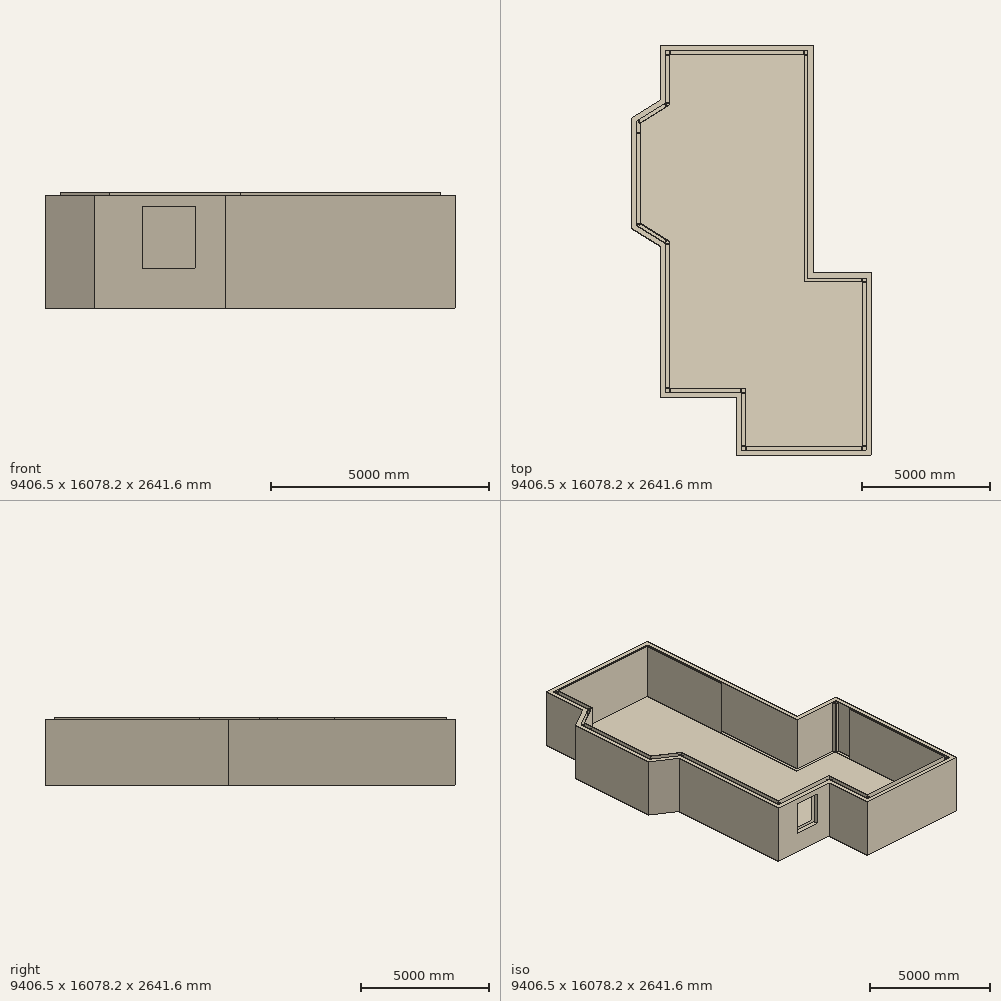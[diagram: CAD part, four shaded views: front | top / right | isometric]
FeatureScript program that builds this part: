
annotation { "Feature Type Name" : "Feature", "Feature Type Description" : "" }
export const myFeature = defineFeature(function(context is Context, id is Id, definition is map)
    precondition{}
    {
        {
            var Q0;
            Q0=qCreatedBy(makeId("Top.planeOp"),FACE);
            var sketch = newSketch(context, id + "F0", { "sketchPlane" : qUnion([Q0])});
            skLineSegment(sketch, "E0", {"start": v(-8280.4, 16078.2) * mm, "end": v(-2286, 16078.2) * mm});
            skLineSegment(sketch, "E1", {"start": v(-2286, 16078.2) * mm, "end": v(-2286, 7162.8) * mm});
            skLineSegment(sketch, "E2", {"start": v(-2286, 7162.8) * mm, "end": v(0, 7162.8) * mm});
            skLineSegment(sketch, "E3", {"start": v(0, 7162.8) * mm, "end": v(0, 0) * mm});
            skLineSegment(sketch, "E4", {"start": v(0, 0) * mm, "end": v(-5283.2, 0) * mm});
            skLineSegment(sketch, "E5", {"start": v(-5283.2, 0) * mm, "end": v(-5283.2, 2286) * mm});
            skLineSegment(sketch, "E6", {"start": v(-5283.2, 2286) * mm, "end": v(-8280.4, 2286) * mm});
            skLineSegment(sketch, "E7", {"start": v(-8280.4, 2286) * mm, "end": v(-8280.4, 8201.03) * mm});
            skLineSegment(sketch, "E8", {"start": v(-8280.4, 8201.03) * mm, "end": v(-9406.5, 8900.32) * mm});
            skLineSegment(sketch, "E9", {"start": v(-9406.5, 8900.32) * mm, "end": v(-9406.5, 13223.08) * mm});
            skLineSegment(sketch, "E10", {"start": v(-9406.5, 13223.08) * mm, "end": v(-8280.4, 13922.38) * mm});
            skLineSegment(sketch, "E11", {"start": v(-8280.4, 13922.38) * mm, "end": v(-8280.4, 16078.2) * mm});
            skSolve(sketch);
        }
        {
            var Q0;
            Q0=qSketchRegion(id+"F0",true);
            extrude(context, id + "F1", {"entities" : qUnion([Q0]), "depth" : 2578.1 * mm});
        }
        {
            var Q0;
            Q0=makeQuery(id+"F1.opExtrude","CAP_FACE",FACE,{"disambiguationData":[OSD([sQuery(id+"F0.wireOp",EDGE,"E0"),sQuery(id+"F0.wireOp",EDGE,"E1"),sQuery(id+"F0.wireOp",EDGE,"E2"),sQuery(id+"F0.wireOp",EDGE,"E3"),sQuery(id+"F0.wireOp",EDGE,"E4"),sQuery(id+"F0.wireOp",EDGE,"E5"),sQuery(id+"F0.wireOp",EDGE,"E6"),sQuery(id+"F0.wireOp",EDGE,"E7"),sQuery(id+"F0.wireOp",EDGE,"E8"),sQuery(id+"F0.wireOp",EDGE,"E9"),sQuery(id+"F0.wireOp",EDGE,"E10"),sQuery(id+"F0.wireOp",EDGE,"E11")])],"isStart":false});
            shell(context, id + "F2", {"entities" : qUnion([Q0]), "thickness" : 203.2 * mm});
        }
        {
            var Q0;
            Q0=makeQuery(id+"F2.opShell","OFFSET_FACE",FACE,{"disambiguationData":[OSD([sQuery(id+"F0.wireOp",EDGE,"E6")])]});
            var sketch = newSketch(context, id + "F3", { "sketchPlane" : qUnion([Q0])});
            skLineSegment(sketch, "E12.bottom", {"start": v(5969, 2324.1) * mm, "end": v(7188.2, 2324.1) * mm});
            skLineSegment(sketch, "E12.top", {"start": v(5969, 901.7) * mm, "end": v(7188.2, 901.7) * mm});
            skLineSegment(sketch, "E12.left", {"start": v(5969, 2324.1) * mm, "end": v(5969, 901.7) * mm});
            skLineSegment(sketch, "E12.right", {"start": v(7188.2, 2324.1) * mm, "end": v(7188.2, 901.7) * mm});
            skPoint(sketch, "E13", {"position": v(6578.6, 2324.1) * mm});
            skSolve(sketch);
        }
        {
            var Q0;
            Q0=makeQuery(id+"F2.opShell","OFFSET_FACE",FACE,{"disambiguationData":[OSD([sQuery(id+"F0.wireOp",EDGE,"E0"),sQuery(id+"F0.wireOp",EDGE,"E1"),sQuery(id+"F0.wireOp",EDGE,"E2"),sQuery(id+"F0.wireOp",EDGE,"E3"),sQuery(id+"F0.wireOp",EDGE,"E4"),sQuery(id+"F0.wireOp",EDGE,"E5"),sQuery(id+"F0.wireOp",EDGE,"E6"),sQuery(id+"F0.wireOp",EDGE,"E7"),sQuery(id+"F0.wireOp",EDGE,"E8"),sQuery(id+"F0.wireOp",EDGE,"E9"),sQuery(id+"F0.wireOp",EDGE,"E10"),sQuery(id+"F0.wireOp",EDGE,"E11")])]});
            var sketch = newSketch(context, id + "F4", { "sketchPlane" : qUnion([Q0])});
            skLineSegment(sketch, "E14.bottom", {"start": v(-8077.2, 13811.9) * mm, "end": v(-7937.5, 13811.9) * mm});
            skLineSegment(sketch, "E14.top", {"start": v(-8077.2, 13850) * mm, "end": v(-7937.5, 13850) * mm});
            skLineSegment(sketch, "E14.left", {"start": v(-8077.2, 13811.9) * mm, "end": v(-8077.2, 13850) * mm});
            skLineSegment(sketch, "E14.right", {"start": v(-7937.5, 13811.9) * mm, "end": v(-7937.5, 13850) * mm});
            skLineSegment(sketch, "E15.bottom", {"start": v(-7934.96, 15875) * mm, "end": v(-7896.86, 15875) * mm});
            skLineSegment(sketch, "E15.top", {"start": v(-7934.96, 15735.3) * mm, "end": v(-7896.86, 15735.3) * mm});
            skLineSegment(sketch, "E15.left", {"start": v(-7934.96, 15875) * mm, "end": v(-7934.96, 15735.3) * mm});
            skLineSegment(sketch, "E15.right", {"start": v(-7896.86, 15875) * mm, "end": v(-7896.86, 15735.3) * mm});
            skLineSegment(sketch, "E16.bottom", {"start": v(-8077.2, 15694.66) * mm, "end": v(-7937.5, 15694.66) * mm});
            skLineSegment(sketch, "E16.top", {"start": v(-8077.2, 15732.76) * mm, "end": v(-7937.5, 15732.76) * mm});
            skLineSegment(sketch, "E16.left", {"start": v(-8077.2, 15694.66) * mm, "end": v(-8077.2, 15732.76) * mm});
            skLineSegment(sketch, "E16.right", {"start": v(-7937.5, 15694.66) * mm, "end": v(-7937.5, 15732.76) * mm});
            skLineSegment(sketch, "E17.bottom", {"start": v(-2631.44, 15875) * mm, "end": v(-2669.54, 15875) * mm});
            skLineSegment(sketch, "E17.top", {"start": v(-2631.44, 15735.3) * mm, "end": v(-2669.54, 15735.3) * mm});
            skLineSegment(sketch, "E17.left", {"start": v(-2631.44, 15875) * mm, "end": v(-2631.44, 15735.3) * mm});
            skLineSegment(sketch, "E17.right", {"start": v(-2669.54, 15875) * mm, "end": v(-2669.54, 15735.3) * mm});
            skLineSegment(sketch, "E18.bottom", {"start": v(-2489.2, 15694.66) * mm, "end": v(-2628.9, 15694.66) * mm});
            skLineSegment(sketch, "E18.top", {"start": v(-2489.2, 15732.76) * mm, "end": v(-2628.9, 15732.76) * mm});
            skLineSegment(sketch, "E18.left", {"start": v(-2489.2, 15694.66) * mm, "end": v(-2489.2, 15732.76) * mm});
            skLineSegment(sketch, "E18.right", {"start": v(-2628.9, 15694.66) * mm, "end": v(-2628.9, 15732.76) * mm});
            skLineSegment(sketch, "E19", {"start": v(-8078.22, 13808.73) * mm, "end": v(-8110.59, 13788.64) * mm});
            skLineSegment(sketch, "E20", {"start": v(-8110.59, 13788.64) * mm, "end": v(-8036.89, 13669.96) * mm});
            skLineSegment(sketch, "E21", {"start": v(-8036.89, 13669.96) * mm, "end": v(-8004.52, 13690.06) * mm});
            skLineSegment(sketch, "E22", {"start": v(-8004.52, 13690.06) * mm, "end": v(-8078.22, 13808.73) * mm});
            skLineSegment(sketch, "E23.bottom", {"start": v(-9203.3, 12669.47) * mm, "end": v(-9063.6, 12669.47) * mm});
            skLineSegment(sketch, "E23.top", {"start": v(-9203.3, 12631.37) * mm, "end": v(-9063.6, 12631.37) * mm});
            skLineSegment(sketch, "E23.left", {"start": v(-9203.3, 12669.47) * mm, "end": v(-9203.3, 12631.37) * mm});
            skLineSegment(sketch, "E23.right", {"start": v(-9063.6, 12669.47) * mm, "end": v(-9063.6, 12631.37) * mm});
            skLineSegment(sketch, "E24", {"start": v(-9162.3, 13135.53) * mm, "end": v(-9129.94, 13155.63) * mm});
            skLineSegment(sketch, "E25", {"start": v(-9129.94, 13155.63) * mm, "end": v(-9056.24, 13036.95) * mm});
            skLineSegment(sketch, "E26", {"start": v(-9056.24, 13036.95) * mm, "end": v(-9088.6, 13016.85) * mm});
            skLineSegment(sketch, "E27", {"start": v(-9088.6, 13016.85) * mm, "end": v(-9162.3, 13135.53) * mm});
            skLineSegment(sketch, "E28", {"start": v(-9162.3, 8987.87) * mm, "end": v(-9088.6, 9106.55) * mm});
            skLineSegment(sketch, "E29", {"start": v(-9088.6, 9106.55) * mm, "end": v(-9056.24, 9086.45) * mm});
            skLineSegment(sketch, "E30", {"start": v(-9056.24, 9086.45) * mm, "end": v(-9129.94, 8967.77) * mm});
            skLineSegment(sketch, "E31", {"start": v(-9129.94, 8967.77) * mm, "end": v(-9162.3, 8987.87) * mm});
            skLineSegment(sketch, "E32", {"start": v(-8109.57, 8334.13) * mm, "end": v(-8077.2, 8314.03) * mm});
            skLineSegment(sketch, "E33", {"start": v(-8077.2, 8314.03) * mm, "end": v(-8003.5, 8432.71) * mm});
            skLineSegment(sketch, "E34", {"start": v(-8003.5, 8432.71) * mm, "end": v(-8035.87, 8452.81) * mm});
            skLineSegment(sketch, "E35", {"start": v(-8035.87, 8452.81) * mm, "end": v(-8109.57, 8334.13) * mm});
            skLineSegment(sketch, "E36.bottom", {"start": v(-9203.3, 9061.59) * mm, "end": v(-9063.6, 9061.59) * mm});
            skLineSegment(sketch, "E36.top", {"start": v(-9203.3, 9099.69) * mm, "end": v(-9063.6, 9099.69) * mm});
            skLineSegment(sketch, "E36.left", {"start": v(-9203.3, 9061.59) * mm, "end": v(-9203.3, 9099.69) * mm});
            skLineSegment(sketch, "E36.right", {"start": v(-9063.6, 9061.59) * mm, "end": v(-9063.6, 9099.69) * mm});
            skLineSegment(sketch, "E37.bottom", {"start": v(-8077.2, 8311.5) * mm, "end": v(-7937.5, 8311.5) * mm});
            skLineSegment(sketch, "E37.top", {"start": v(-8077.2, 8273.4) * mm, "end": v(-7937.5, 8273.4) * mm});
            skLineSegment(sketch, "E37.left", {"start": v(-8077.2, 8311.5) * mm, "end": v(-8077.2, 8273.4) * mm});
            skLineSegment(sketch, "E37.right", {"start": v(-7937.5, 8311.5) * mm, "end": v(-7937.5, 8273.4) * mm});
            skLineSegment(sketch, "E38.bottom", {"start": v(-8077.2, 2631.44) * mm, "end": v(-7937.5, 2631.44) * mm});
            skLineSegment(sketch, "E38.top", {"start": v(-8077.2, 2669.54) * mm, "end": v(-7937.5, 2669.54) * mm});
            skLineSegment(sketch, "E38.left", {"start": v(-8077.2, 2631.44) * mm, "end": v(-8077.2, 2669.54) * mm});
            skLineSegment(sketch, "E38.right", {"start": v(-7937.5, 2631.44) * mm, "end": v(-7937.5, 2669.54) * mm});
            skLineSegment(sketch, "E39.bottom", {"start": v(-7896.86, 2489.2) * mm, "end": v(-7934.96, 2489.2) * mm});
            skLineSegment(sketch, "E39.top", {"start": v(-7896.86, 2628.9) * mm, "end": v(-7934.96, 2628.9) * mm});
            skLineSegment(sketch, "E39.left", {"start": v(-7896.86, 2489.2) * mm, "end": v(-7896.86, 2628.9) * mm});
            skLineSegment(sketch, "E39.right", {"start": v(-7934.96, 2489.2) * mm, "end": v(-7934.96, 2628.9) * mm});
            skLineSegment(sketch, "E40.bottom", {"start": v(-5082.54, 2489.2) * mm, "end": v(-5120.64, 2489.2) * mm});
            skLineSegment(sketch, "E40.top", {"start": v(-5082.54, 2628.9) * mm, "end": v(-5120.64, 2628.9) * mm});
            skLineSegment(sketch, "E40.left", {"start": v(-5082.54, 2489.2) * mm, "end": v(-5082.54, 2628.9) * mm});
            skLineSegment(sketch, "E40.right", {"start": v(-5120.64, 2489.2) * mm, "end": v(-5120.64, 2628.9) * mm});
            skLineSegment(sketch, "E41.top", {"start": v(-5080, 2448.56) * mm, "end": v(-4940.3, 2448.56) * mm});
            skLineSegment(sketch, "E41.right", {"start": v(-4940.3, 2486.66) * mm, "end": v(-4940.3, 2448.56) * mm});
            skLineSegment(sketch, "E42.bottom", {"start": v(-5080, 345.44) * mm, "end": v(-4940.3, 345.44) * mm});
            skLineSegment(sketch, "E42.top", {"start": v(-5080, 383.54) * mm, "end": v(-4940.3, 383.54) * mm});
            skLineSegment(sketch, "E42.left", {"start": v(-5080, 345.44) * mm, "end": v(-5080, 383.54) * mm});
            skLineSegment(sketch, "E42.right", {"start": v(-4940.3, 345.44) * mm, "end": v(-4940.3, 383.54) * mm});
            skLineSegment(sketch, "E43.bottom", {"start": v(-4937.76, 203.2) * mm, "end": v(-4899.66, 203.2) * mm});
            skLineSegment(sketch, "E43.top", {"start": v(-4937.76, 342.9) * mm, "end": v(-4899.66, 342.9) * mm});
            skLineSegment(sketch, "E43.left", {"start": v(-4937.76, 203.2) * mm, "end": v(-4937.76, 342.9) * mm});
            skLineSegment(sketch, "E43.right", {"start": v(-4899.66, 203.2) * mm, "end": v(-4899.66, 342.9) * mm});
            skLineSegment(sketch, "E44.bottom", {"start": v(-383.54, 203.2) * mm, "end": v(-345.44, 203.2) * mm});
            skLineSegment(sketch, "E44.top", {"start": v(-383.54, 342.9) * mm, "end": v(-345.44, 342.9) * mm});
            skLineSegment(sketch, "E44.left", {"start": v(-383.54, 203.2) * mm, "end": v(-383.54, 342.9) * mm});
            skLineSegment(sketch, "E44.right", {"start": v(-345.44, 203.2) * mm, "end": v(-345.44, 342.9) * mm});
            skLineSegment(sketch, "E45.bottom", {"start": v(-203.2, 345.44) * mm, "end": v(-342.9, 345.44) * mm});
            skLineSegment(sketch, "E45.top", {"start": v(-203.2, 383.54) * mm, "end": v(-342.9, 383.54) * mm});
            skLineSegment(sketch, "E45.left", {"start": v(-203.2, 345.44) * mm, "end": v(-203.2, 383.54) * mm});
            skLineSegment(sketch, "E45.right", {"start": v(-342.9, 345.44) * mm, "end": v(-342.9, 383.54) * mm});
            skLineSegment(sketch, "E46.bottom", {"start": v(-203.2, 6779.26) * mm, "end": v(-342.9, 6779.26) * mm});
            skLineSegment(sketch, "E46.top", {"start": v(-203.2, 6817.36) * mm, "end": v(-342.9, 6817.36) * mm});
            skLineSegment(sketch, "E46.left", {"start": v(-203.2, 6779.26) * mm, "end": v(-203.2, 6817.36) * mm});
            skLineSegment(sketch, "E46.right", {"start": v(-342.9, 6779.26) * mm, "end": v(-342.9, 6817.36) * mm});
            skLineSegment(sketch, "E47.bottom", {"start": v(-345.44, 6959.6) * mm, "end": v(-383.54, 6959.6) * mm});
            skLineSegment(sketch, "E47.top", {"start": v(-345.44, 6819.9) * mm, "end": v(-383.54, 6819.9) * mm});
            skLineSegment(sketch, "E47.left", {"start": v(-345.44, 6959.6) * mm, "end": v(-345.44, 6819.9) * mm});
            skLineSegment(sketch, "E47.right", {"start": v(-383.54, 6959.6) * mm, "end": v(-383.54, 6819.9) * mm});
            skLineSegment(sketch, "E48", {"start": v(-4940.3, 2486.66) * mm, "end": v(-5080, 2486.66) * mm});
            skLineSegment(sketch, "E49", {"start": v(-5080, 2486.66) * mm, "end": v(-5080, 2448.56) * mm});
            skLineSegment(sketch, "E50", {"start": v(-9203.3, 13110.07) * mm, "end": v(-9045.7, 12987.43) * mm, "construction": true});
            skLineSegment(sketch, "E51", {"start": v(-9045.7, 12987.43) * mm, "end": v(-9104.83, 13171.22) * mm, "construction": true});
            skLineSegment(sketch, "E52", {"start": v(-9104.83, 13171.22) * mm, "end": v(-9203.3, 12968.55) * mm, "construction": true});
            skLineSegment(sketch, "E53", {"start": v(-9203.3, 12968.55) * mm, "end": v(-9045.7, 12987.43) * mm, "construction": true});
            skSolve(sketch);
        }
        {
            var Q0;
            Q0=qSketchRegion(id+"F3",true);
            var Q1;
            Q1=makeQuery(id+"FwcOo8eikqoZCvb_1.opExtrude","SWEPT_FACE",FACE,{"disambiguationData":[OSD([sQuery(id+"F7.wireOp",EDGE,"E55.top"),sQuery(id+"F7.wireOp",EDGE,"E63")])]});
            extrude(context, id + "F5", {"entities" : qUnion([Q0]), "operationType" : NewBodyOperationType.REMOVE, "endBound" : BoundingType.UP_TO_NEXT, "oppositeDirection" : true, "depth" : 25.4 * mm});
        }
        {
            var Q0;
            Q0=qSketchRegion(id+"F4",true);
            extrude(context, id + "F6", {"entities" : qUnion([Q0]), "operationType" : NewBodyOperationType.ADD, "depth" : 2349.5 * mm});
        }
        {
            var Q0;
            Q0=makeQuery(id+"F2.opShell","OFFSET_FACE",FACE,{"disambiguationData":[OSD([sQuery(id+"F0.wireOp",EDGE,"E0"),sQuery(id+"F0.wireOp",EDGE,"E1"),sQuery(id+"F0.wireOp",EDGE,"E2"),sQuery(id+"F0.wireOp",EDGE,"E3"),sQuery(id+"F0.wireOp",EDGE,"E4"),sQuery(id+"F0.wireOp",EDGE,"E5"),sQuery(id+"F0.wireOp",EDGE,"E6"),sQuery(id+"F0.wireOp",EDGE,"E7"),sQuery(id+"F0.wireOp",EDGE,"E8"),sQuery(id+"F0.wireOp",EDGE,"E9"),sQuery(id+"F0.wireOp",EDGE,"E10"),sQuery(id+"F0.wireOp",EDGE,"E11")])]});
            var sketch = newSketch(context, id + "F7", { "sketchPlane" : qUnion([Q0])});
            skLineSegment(sketch, "E54.bottom", {"start": v(-7937.5, 8391.73) * mm, "end": v(-7924.8, 8391.73) * mm, "construction": true});
            skLineSegment(sketch, "E54.top", {"start": v(-7937.5, 2641.6) * mm, "end": v(-7924.8, 2641.6) * mm, "construction": true});
            skLineSegment(sketch, "E54.left", {"start": v(-7937.5, 8391.73) * mm, "end": v(-7937.5, 2641.6) * mm});
            skLineSegment(sketch, "E54.right", {"start": v(-7924.8, 8391.73) * mm, "end": v(-7924.8, 2641.6) * mm});
            skLineSegment(sketch, "E55.bottom", {"start": v(-7924.8, 2628.9) * mm, "end": v(-4940.3, 2628.9) * mm});
            skLineSegment(sketch, "E55.top", {"start": v(-7924.8, 2641.6) * mm, "end": v(-4940.3, 2641.6) * mm});
            skLineSegment(sketch, "E55.left", {"start": v(-7924.8, 2628.9) * mm, "end": v(-7924.8, 2641.6) * mm, "construction": true});
            skLineSegment(sketch, "E55.right", {"start": v(-4940.3, 2628.9) * mm, "end": v(-4940.3, 2641.6) * mm, "construction": true});
            skLineSegment(sketch, "E56", {"start": v(-7924.8, 2628.9) * mm, "end": v(-7937.5, 2628.9) * mm});
            skLineSegment(sketch, "E57", {"start": v(-7937.5, 2628.9) * mm, "end": v(-7937.5, 2641.6) * mm});
            skLineSegment(sketch, "E58.bottom", {"start": v(-4940.3, 2628.9) * mm, "end": v(-4927.6, 2628.9) * mm, "construction": true});
            skLineSegment(sketch, "E58.top", {"start": v(-4940.3, 355.6) * mm, "end": v(-4927.6, 355.6) * mm, "construction": true});
            skLineSegment(sketch, "E58.left", {"start": v(-4940.3, 2628.9) * mm, "end": v(-4940.3, 355.6) * mm});
            skLineSegment(sketch, "E58.right", {"start": v(-4927.6, 2628.9) * mm, "end": v(-4927.6, 355.6) * mm});
            skLineSegment(sketch, "E59.bottom", {"start": v(-4927.6, 342.9) * mm, "end": v(-355.6, 342.9) * mm});
            skLineSegment(sketch, "E59.top", {"start": v(-4927.6, 355.6) * mm, "end": v(-355.6, 355.6) * mm});
            skLineSegment(sketch, "E59.left", {"start": v(-4927.6, 342.9) * mm, "end": v(-4927.6, 355.6) * mm, "construction": true});
            skLineSegment(sketch, "E59.right", {"start": v(-355.6, 342.9) * mm, "end": v(-355.6, 355.6) * mm, "construction": true});
            skLineSegment(sketch, "E60", {"start": v(-4940.3, 355.6) * mm, "end": v(-4940.3, 342.9) * mm});
            skLineSegment(sketch, "E61", {"start": v(-4940.3, 342.9) * mm, "end": v(-4927.6, 342.9) * mm});
            skLineSegment(sketch, "E62", {"start": v(-4927.6, 2628.9) * mm, "end": v(-4927.6, 2641.6) * mm});
            skLineSegment(sketch, "E63", {"start": v(-4940.3, 2641.6) * mm, "end": v(-4927.6, 2641.6) * mm});
            skLineSegment(sketch, "E64.bottom", {"start": v(-355.6, 355.6) * mm, "end": v(-342.9, 355.6) * mm, "construction": true});
            skLineSegment(sketch, "E64.top", {"start": v(-355.6, 6019.58) * mm, "end": v(-342.9, 6019.58) * mm});
            skLineSegment(sketch, "E64.left", {"start": v(-355.6, 355.6) * mm, "end": v(-355.6, 6019.58) * mm});
            skLineSegment(sketch, "E64.right", {"start": v(-342.9, 355.6) * mm, "end": v(-342.9, 6019.58) * mm});
            skLineSegment(sketch, "E65", {"start": v(-355.6, 342.9) * mm, "end": v(-342.9, 342.9) * mm});
            skLineSegment(sketch, "E66", {"start": v(-342.9, 342.9) * mm, "end": v(-342.9, 355.6) * mm});
            skLineSegment(sketch, "E67", {"start": v(-7937.5, 8391.73) * mm, "end": v(-9063.6, 9091.02) * mm});
            skLineSegment(sketch, "E68", {"start": v(-9063.6, 9091.02) * mm, "end": v(-9063.6, 13032.38) * mm});
            skLineSegment(sketch, "E69", {"start": v(-9063.6, 13032.38) * mm, "end": v(-7937.5, 13731.67) * mm});
            skLineSegment(sketch, "E70", {"start": v(-7937.5, 13731.67) * mm, "end": v(-7937.5, 15735.3) * mm});
            skLineSegment(sketch, "E71", {"start": v(-7937.5, 15735.3) * mm, "end": v(-2628.9, 15735.3) * mm});
            skLineSegment(sketch, "E72", {"start": v(-2628.9, 15735.3) * mm, "end": v(-2628.9, 11339.58) * mm});
            skLineSegment(sketch, "E73", {"start": v(-2628.9, 11339.58) * mm, "end": v(-2641.6, 11339.58) * mm});
            skLineSegment(sketch, "E74", {"start": v(-2641.6, 11339.58) * mm, "end": v(-2641.6, 15722.6) * mm});
            skLineSegment(sketch, "E75", {"start": v(-2641.6, 15722.6) * mm, "end": v(-7924.8, 15722.6) * mm});
            skLineSegment(sketch, "E76", {"start": v(-7924.8, 15722.6) * mm, "end": v(-7924.8, 13724.61) * mm});
            skLineSegment(sketch, "E77", {"start": v(-7924.8, 13724.61) * mm, "end": v(-9050.9, 13025.32) * mm});
            skLineSegment(sketch, "E78", {"start": v(-9050.9, 13025.32) * mm, "end": v(-9050.9, 9098.08) * mm});
            skLineSegment(sketch, "E79", {"start": v(-9050.9, 9098.08) * mm, "end": v(-7924.8, 8398.79) * mm});
            skLineSegment(sketch, "E80", {"start": v(-8493.85, 8752.16) * mm, "end": v(-8500.55, 8741.37) * mm, "construction": true});
            skLineSegment(sketch, "E81", {"start": v(-9063.6, 11061.7) * mm, "end": v(-9050.9, 11061.7) * mm, "construction": true});
            skLineSegment(sketch, "E82", {"start": v(-8487.85, 13374.97) * mm, "end": v(-8494.55, 13385.75) * mm, "construction": true});
            skLineSegment(sketch, "E83", {"start": v(-7924.8, 15722.6) * mm, "end": v(-7937.5, 15722.6) * mm, "construction": true});
            skLineSegment(sketch, "E84", {"start": v(-2641.6, 15735.3) * mm, "end": v(-2641.6, 15722.6) * mm, "construction": true});
            skLineSegment(sketch, "E85", {"start": v(-7924.8, 8391.73) * mm, "end": v(-7924.8, 8398.79) * mm});
            skSolve(sketch);
        }
        {
            var Q0;
            Q0=qSketchRegion(id+"F7",true);
            extrude(context, id + "F8", {"entities" : qUnion([Q0]), "depth" : 12 * 203.2 * mm});
        }
        {
            var Q0;
            Q0=qSketchRegion(id+"F3",true);
            var Q1;
            Q1=makeQuery(id+"F8.opExtrude","SWEPT_FACE",FACE,{"disambiguationData":[OSD([sQuery(id+"F7.wireOp",EDGE,"E55.top"),sQuery(id+"F7.wireOp",EDGE,"E63")])]});
            extrude(context, id + "F9", {"entities" : qUnion([Q0]), "operationType" : NewBodyOperationType.REMOVE, "endBound" : BoundingType.UP_TO_SURFACE, "endBoundEntityFace" : qUnion([Q1]), "depth" : 25.4 * mm});
        }
        {
            var Q0;
            Q0=qCreatedBy(makeId("Top.planeOp"),FACE);
            var sketch = newSketch(context, id + "F10", { "sketchPlane" : qUnion([Q0])});
            skLineSegment(sketch, "E86", {"start": v(-8077.2, 2489.2) * mm, "end": v(-8077.2, 8314.03) * mm});
            skLineSegment(sketch, "E87", {"start": v(-8077.2, 8314.03) * mm, "end": v(-9203.3, 9013.33) * mm});
            skLineSegment(sketch, "E88", {"start": v(-9203.3, 9013.33) * mm, "end": v(-9203.3, 13110.07) * mm});
            skLineSegment(sketch, "E89", {"start": v(-9203.3, 13110.07) * mm, "end": v(-8077.2, 13809.37) * mm});
            skLineSegment(sketch, "E90", {"start": v(-8077.2, 13809.37) * mm, "end": v(-8077.2, 15875) * mm});
            skLineSegment(sketch, "E91", {"start": v(-8077.2, 15875) * mm, "end": v(-2489.2, 15875) * mm});
            skLineSegment(sketch, "E92", {"start": v(-2489.2, 15875) * mm, "end": v(-2489.2, 11339.58) * mm});
            skLineSegment(sketch, "E93", {"start": v(-2489.2, 11339.58) * mm, "end": v(-2628.9, 11339.58) * mm});
            skLineSegment(sketch, "E94", {"start": v(-2628.9, 11339.58) * mm, "end": v(-2628.9, 15735.3) * mm});
            skLineSegment(sketch, "E95", {"start": v(-7937.5, 15735.3) * mm, "end": v(-7937.5, 13731.67) * mm});
            skLineSegment(sketch, "E96", {"start": v(-7937.5, 13731.67) * mm, "end": v(-9063.6, 13032.38) * mm});
            skLineSegment(sketch, "E97", {"start": v(-9063.6, 13032.38) * mm, "end": v(-9063.6, 9091.02) * mm});
            skLineSegment(sketch, "E98", {"start": v(-9063.6, 9091.02) * mm, "end": v(-7937.5, 8391.73) * mm});
            skLineSegment(sketch, "E99", {"start": v(-7937.5, 8391.73) * mm, "end": v(-7937.5, 2628.9) * mm});
            skLineSegment(sketch, "E100", {"start": v(-7937.5, 2628.9) * mm, "end": v(-4940.3, 2628.9) * mm});
            skLineSegment(sketch, "E101", {"start": v(-4940.3, 2628.9) * mm, "end": v(-4940.3, 342.9) * mm});
            skLineSegment(sketch, "E102", {"start": v(-4940.3, 342.9) * mm, "end": v(-342.9, 342.9) * mm});
            skLineSegment(sketch, "E103", {"start": v(-342.9, 342.9) * mm, "end": v(-342.9, 5526.42) * mm});
            skLineSegment(sketch, "E104", {"start": v(-342.9, 5526.42) * mm, "end": v(-203.2, 5526.42) * mm});
            skLineSegment(sketch, "E105", {"start": v(-203.2, 5526.42) * mm, "end": v(-203.2, 203.2) * mm});
            skLineSegment(sketch, "E106", {"start": v(-203.2, 203.2) * mm, "end": v(-5080, 203.2) * mm});
            skLineSegment(sketch, "E107", {"start": v(-5080, 203.2) * mm, "end": v(-5080, 2489.2) * mm});
            skLineSegment(sketch, "E108", {"start": v(-5080, 2489.2) * mm, "end": v(-8077.2, 2489.2) * mm});
            skLineSegment(sketch, "E109", {"start": v(-9203.3, 11061.7) * mm, "end": v(-9063.6, 11061.7) * mm, "construction": true});
            skLineSegment(sketch, "E110", {"start": v(-8566.55, 13341.04) * mm, "end": v(-8640.25, 13459.72) * mm, "construction": true});
            skLineSegment(sketch, "E111", {"start": v(-8077.2, 14842.18) * mm, "end": v(-7937.5, 14842.18) * mm, "construction": true});
            skLineSegment(sketch, "E112", {"start": v(-2489.2, 13607.29) * mm, "end": v(-2628.9, 13607.29) * mm, "construction": true});
            skLineSegment(sketch, "E113", {"start": v(-7937.5, 15735.3) * mm, "end": v(-2628.9, 15735.3) * mm});
            skLineSegment(sketch, "E114", {"start": v(-5283.2, 15735.3) * mm, "end": v(-5283.2, 15875) * mm, "construction": true});
            skLineSegment(sketch, "E115", {"start": v(-8640.25, 8663.68) * mm, "end": v(-8566.55, 8782.36) * mm, "construction": true});
            skLineSegment(sketch, "E116", {"start": v(-7937.5, 5401.62) * mm, "end": v(-8077.2, 5401.62) * mm, "construction": true});
            skLineSegment(sketch, "E117", {"start": v(-6578.6, 2489.2) * mm, "end": v(-6578.6, 2628.9) * mm, "construction": true});
            skSolve(sketch);
        }
        {
            var Q0;
            Q0=qSketchRegion(id+"F10",true);
            extrude(context, id + "F11", {"entities" : qUnion([Q0]), "depth" : 12.7 * mm});
        }
        {
            var Q0;
            {var subQ102=sQuery(id+"F4.wireOp",EDGE,"E14.bottom");Q0=makeQuery(id+"F4.imprint","IMPRINT",FACE,{"disambiguationData":[TD([[makeQuery(id+"F4.imprint","IMPRINT",EDGE,{"derivedFrom":subQ102}),-1.0]])]});}
            var sketch = newSketch(context, id + "F12", { "sketchPlane" : qUnion([Q0])});
            skLineSegment(sketch, "E118", {"start": v(-7924.8, 2641.6) * mm, "end": v(-7924.8, 8398.79) * mm});
            skLineSegment(sketch, "E119", {"start": v(-7924.8, 8398.79) * mm, "end": v(-9050.9, 9098.08) * mm});
            skLineSegment(sketch, "E120", {"start": v(-9050.9, 9098.08) * mm, "end": v(-9050.9, 13025.32) * mm});
            skLineSegment(sketch, "E121", {"start": v(-9050.9, 13025.32) * mm, "end": v(-7924.8, 13724.61) * mm});
            skLineSegment(sketch, "E122", {"start": v(-7924.8, 13724.61) * mm, "end": v(-7924.8, 15722.6) * mm});
            skLineSegment(sketch, "E123", {"start": v(-7924.8, 15722.6) * mm, "end": v(-2641.6, 15722.6) * mm});
            skLineSegment(sketch, "E124", {"start": v(-2641.6, 15722.6) * mm, "end": v(-2641.6, 6819.9) * mm});
            skLineSegment(sketch, "E125", {"start": v(-2641.6, 6819.9) * mm, "end": v(-355.6, 6819.9) * mm});
            skLineSegment(sketch, "E126", {"start": v(-355.6, 6819.9) * mm, "end": v(-355.6, 355.6) * mm});
            skLineSegment(sketch, "E127", {"start": v(-355.6, 355.6) * mm, "end": v(-4927.6, 355.6) * mm});
            skLineSegment(sketch, "E128", {"start": v(-4927.6, 355.6) * mm, "end": v(-4927.6, 2641.6) * mm});
            skLineSegment(sketch, "E129", {"start": v(-4927.6, 2641.6) * mm, "end": v(-7924.8, 2641.6) * mm});
            skSolve(sketch);
        }
        {
            var Q0;
            Q0 = qSketchRegion(id + "F12", true);
            extrude(context, id + "F13", {"entities" : qUnion([Q0]), "depth" : 12.7 * mm});
        }
    });
